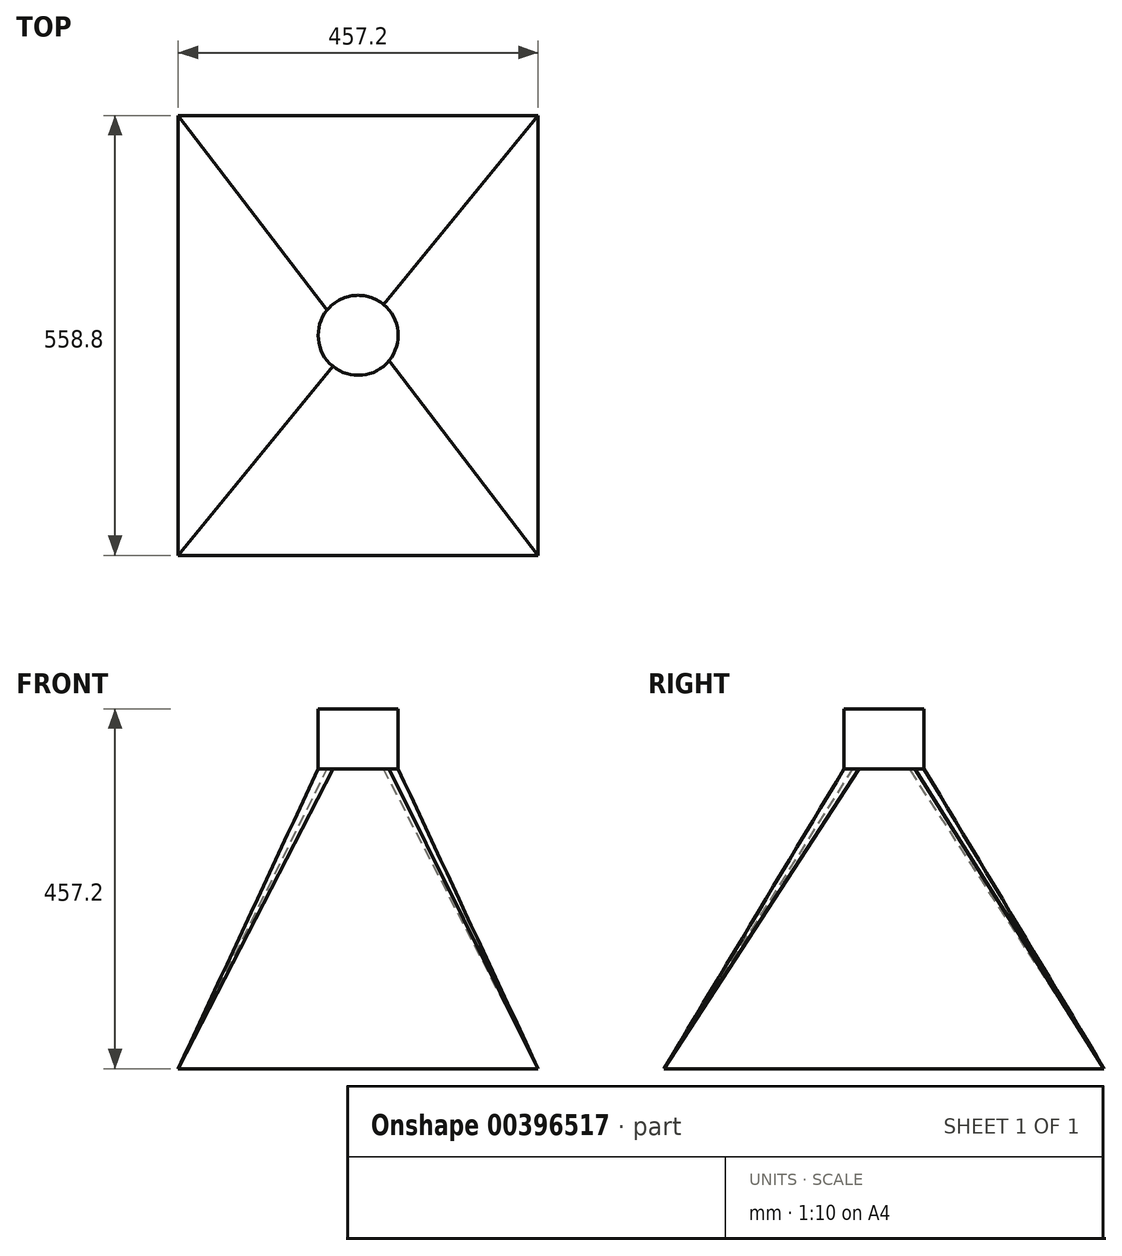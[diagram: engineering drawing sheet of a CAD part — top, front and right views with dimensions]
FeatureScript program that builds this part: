
annotation { "Feature Type Name" : "Feature", "Feature Type Description" : "" }
export const myFeature = defineFeature(function(context is Context, id is Id, definition is map)
    precondition{}
    {
        {
            var Q0;
            Q0=qCreatedBy(makeId("Top.planeOp"),FACE);
            var sketch = newSketch(context, id + "F0", { "sketchPlane" : qUnion([Q0])});
            skLineSegment(sketch, "E0.bottom", {"start": v(0, 0) * mm, "end": v(457.2, 0) * mm});
            skLineSegment(sketch, "E0.top", {"start": v(0, 558.8) * mm, "end": v(457.2, 558.8) * mm});
            skLineSegment(sketch, "E0.left", {"start": v(0, 0) * mm, "end": v(0, 558.8) * mm});
            skLineSegment(sketch, "E0.right", {"start": v(457.2, 0) * mm, "end": v(457.2, 558.8) * mm});
            skSolve(sketch);
        }
        {
            var Q0;
            Q0=qCreatedBy(makeId("Top.planeOp"),FACE);
            cPlane(context, id + "F1", {"entities" : qUnion([Q0]), "cplaneType" : CPlaneType.OFFSET, "offset" : 381 * mm, "width" : 152.4 * mm, "height" : 152.4 * mm});
        }
        {
            var Q0;
            Q0=qCreatedBy(id+"F1.planeOp",FACE);
            var sketch = newSketch(context, id + "F2", { "sketchPlane" : qUnion([Q0])});
            skCircle(sketch, "E1", {"center": v(228.6, 279.4) * mm, "radius": 50.8 * mm});
            skSolve(sketch);
        }
        {
            var Q0;
            Q0=makeQuery(id+"F0.imprint","IMPRINT",FACE,{"disambiguationData":[TD([[makeQuery(id+"F0.imprint","IMPRINT",EDGE,{"derivedFrom":sQuery(id+"F0.wireOp",EDGE,"E0.bottom")}),1.0]])]});
            var Q1;
            Q1=makeQuery(id+"F2.imprint","IMPRINT",FACE,{"disambiguationData":[TD([[makeQuery(id+"F2.imprint","IMPRINT",EDGE,{"derivedFrom":sQuery(id+"F2.wireOp",EDGE,"E1")}),1.0]])]});
            loft(context, id + "F3", {"sheetProfilesArray" : [{ "sheetProfileEntities" : qUnion([Q0]) }, { "sheetProfileEntities" : qUnion([Q1]) }]});
        }
        {
            var Q0;
            Q0=makeQuery(id+"F3.opLoft","CAP_FACE",FACE,{"disambiguationData":[OSD([makeQuery(id+"F2.imprint","IMPRINT",FACE,{"disambiguationData":[TD([[makeQuery(id+"F2.imprint","IMPRINT",EDGE,{"derivedFrom":sQuery(id+"F2.wireOp",EDGE,"E1")}),1.0]])]})])],"isStart":true});
            extrude(context, id + "F4", {"entities" : qUnion([Q0]), "operationType" : NewBodyOperationType.ADD, "depth" : 76.2 * mm});
        }
    });
